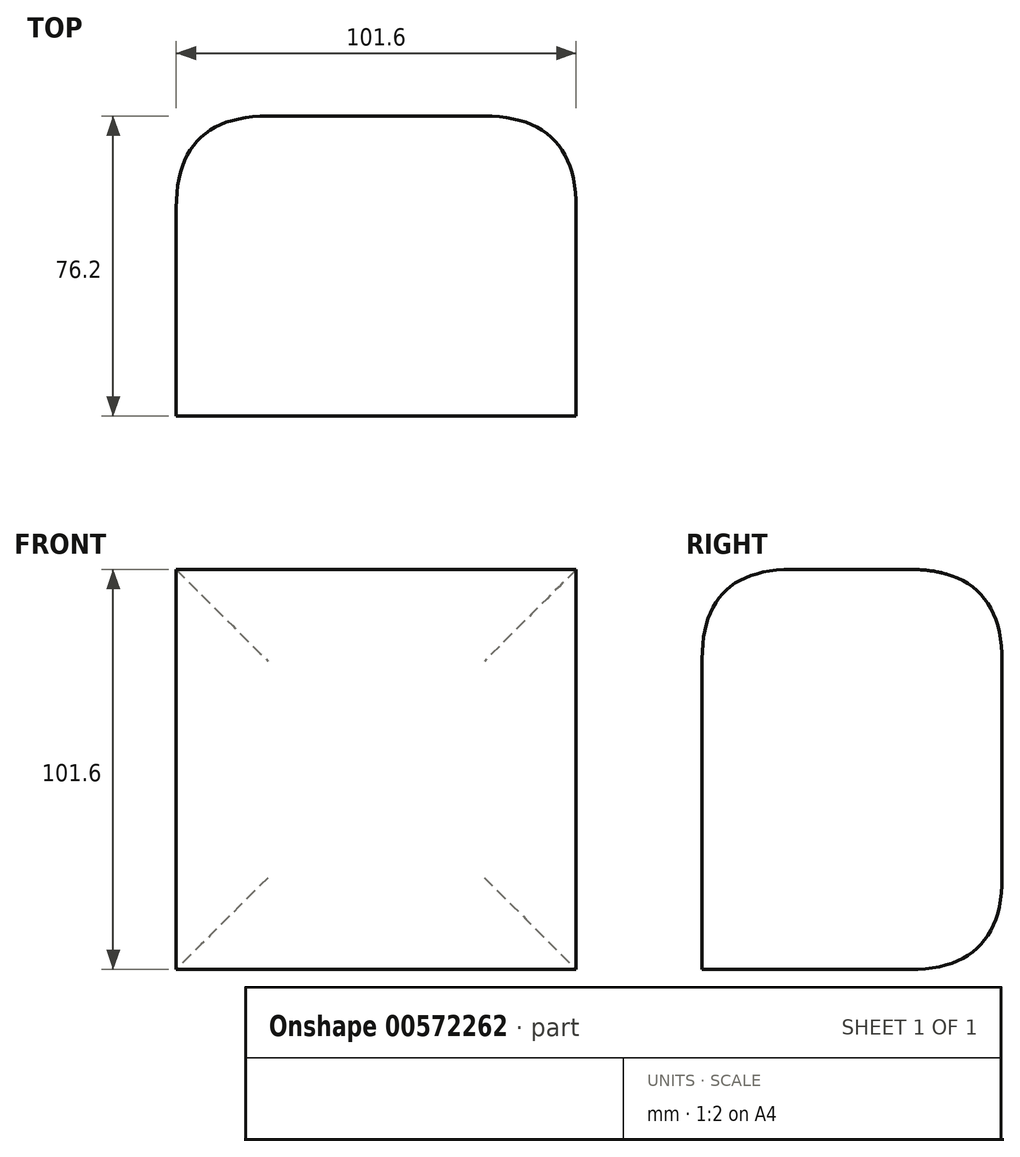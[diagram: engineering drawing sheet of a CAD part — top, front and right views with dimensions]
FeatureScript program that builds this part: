
annotation { "Feature Type Name" : "Feature", "Feature Type Description" : "" }
export const myFeature = defineFeature(function(context is Context, id is Id, definition is map)
    precondition{}
    {
        {
            var Q0;
            Q0=qCreatedBy(makeId("Front.planeOp"),FACE);
            var sketch = newSketch(context, id + "F0", { "sketchPlane" : qUnion([Q0])});
            skLineSegment(sketch, "E0.bottom", {"start": v(-49.93, -44.28) * mm, "end": v(51.67, -44.28) * mm});
            skLineSegment(sketch, "E0.top", {"start": v(-49.93, 57.32) * mm, "end": v(51.67, 57.32) * mm});
            skLineSegment(sketch, "E0.left", {"start": v(-49.93, -44.28) * mm, "end": v(-49.93, 57.32) * mm});
            skLineSegment(sketch, "E0.right", {"start": v(51.67, -44.28) * mm, "end": v(51.67, 57.32) * mm});
            skSolve(sketch);
        }
        {
            var Q0;
            Q0=makeQuery(id+"F0.imprint","IMPRINT",FACE,{"disambiguationData":[TD([[makeQuery(id+"F0.imprint","IMPRINT",EDGE,{"derivedFrom":sQuery(id+"F0.wireOp",EDGE,"E0.bottom")}),1.0]])]});
            extrude(context, id + "F1", {"entities" : qUnion([Q0]), "depth" : 76.2 * mm, "offsetDistance" : 25.4 * mm});
        }
        {
            var Q0;
            Q0=makeQuery(id+"F1.opExtrude","CAP_EDGE",EDGE,{"disambiguationData":[OSD([sQuery(id+"F0.wireOp",EDGE,"E0.top")])],"isStart":false});
            fillet(context, id + "F2", {"entities" : qUnion([Q0]), "radius" : 22.7 * mm, "tangentPropagation" : true, "rho" : 0.5, "crossSection" : FilletCrossSection.CONIC, "allowEdgeOverflow" : false});
        }
        {
            var Q0;
            Q0=makeQuery(id+"F1.opExtrude","CAP_FACE",FACE,{"disambiguationData":[OSD([sQuery(id+"F0.wireOp",EDGE,"E0.bottom"),sQuery(id+"F0.wireOp",EDGE,"E0.top"),sQuery(id+"F0.wireOp",EDGE,"E0.left"),sQuery(id+"F0.wireOp",EDGE,"E0.right")])],"isStart":true});
            fillet(context, id + "F3", {"entities" : qUnion([Q0]), "radius" : 23.3 * mm, "tangentPropagation" : true, "rho" : 0.5, "crossSection" : FilletCrossSection.CONIC, "allowEdgeOverflow" : false});
        }
    });
